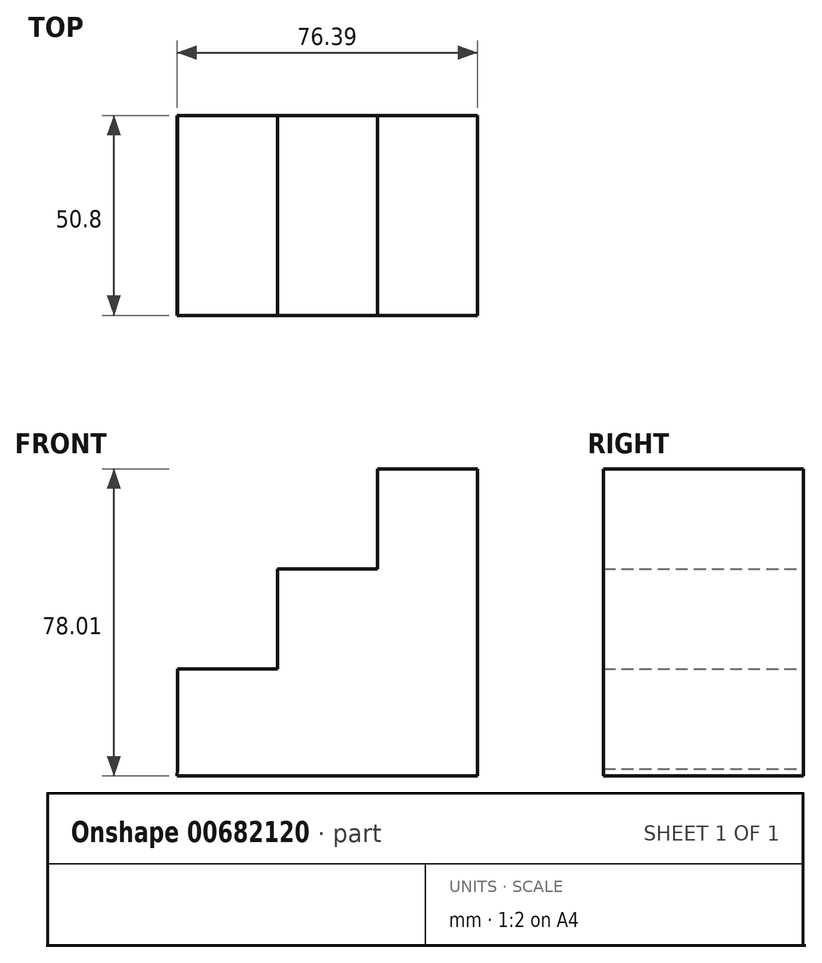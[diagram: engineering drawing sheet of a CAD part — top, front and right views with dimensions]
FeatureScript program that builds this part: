
annotation { "Feature Type Name" : "Feature", "Feature Type Description" : "" }
export const myFeature = defineFeature(function(context is Context, id is Id, definition is map)
    precondition{}
    {
        {
            var Q0;
            Q0=qCreatedBy(makeId("Front.planeOp"),FACE);
            var sketch = newSketch(context, id + "F0", { "sketchPlane" : qUnion([Q0])});
            skLineSegment(sketch, "E0", {"start": v(-38.1, 0) * mm, "end": v(-38.1, 25.4) * mm});
            skLineSegment(sketch, "E1", {"start": v(-38.1, 25.4) * mm, "end": v(-12.7, 25.4) * mm});
            skLineSegment(sketch, "E2", {"start": v(-12.7, 25.4) * mm, "end": v(-12.7, 50.8) * mm});
            skLineSegment(sketch, "E3", {"start": v(-12.7, 50.8) * mm, "end": v(12.7, 50.8) * mm});
            skLineSegment(sketch, "E4", {"start": v(12.7, 50.8) * mm, "end": v(12.7, 76.2) * mm});
            skLineSegment(sketch, "E5", {"start": v(12.7, 76.2) * mm, "end": v(38.1, 76.2) * mm});
            skLineSegment(sketch, "E6", {"start": v(38.1, 76.2) * mm, "end": v(38.1, -1.81) * mm});
            skLineSegment(sketch, "E7", {"start": v(38.1, -1.81) * mm, "end": v(-38.29, -1.81) * mm});
            skLineSegment(sketch, "E8", {"start": v(-38.29, -1.81) * mm, "end": v(-38.1, 0) * mm});
            skSolve(sketch);
        }
        {
            var Q0;
            Q0 = qSketchRegion(id + "F0", true);
            extrude(context, id + "F1", {"entities" : qUnion([Q0]), "depth" : 50.8 * mm, "offsetDistance" : 25.4 * mm});
        }
    });
